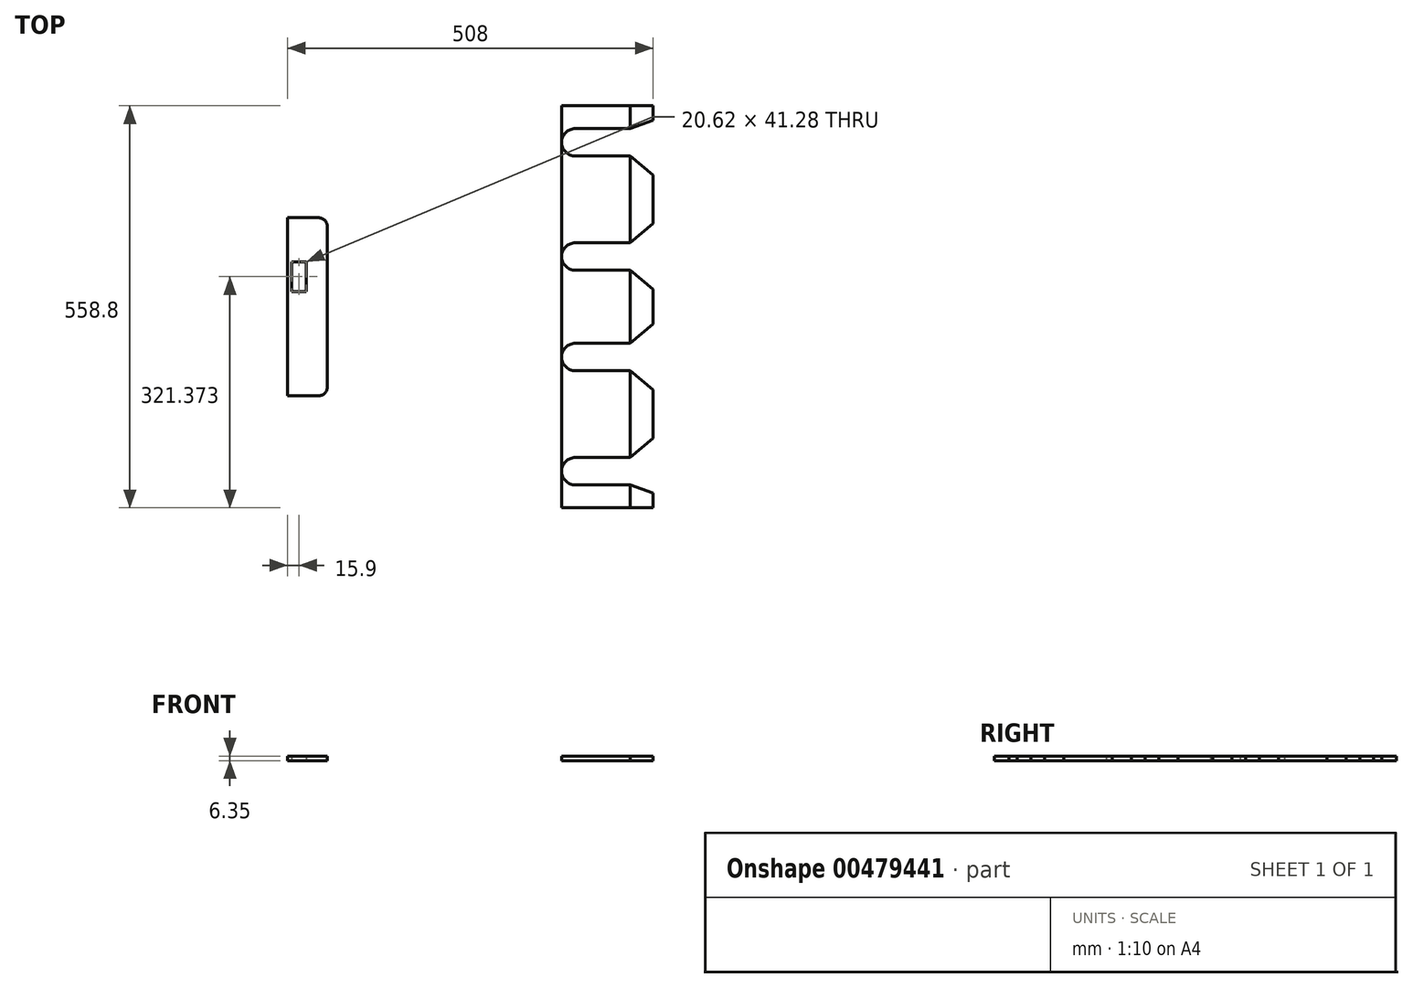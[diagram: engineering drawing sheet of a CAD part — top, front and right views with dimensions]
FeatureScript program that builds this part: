
annotation { "Feature Type Name" : "Feature", "Feature Type Description" : "" }
export const myFeature = defineFeature(function(context is Context, id is Id, definition is map)
    precondition{}
    {
        {
            var Q0;
            Q0=qCreatedBy(makeId("Top.planeOp"),FACE);
            var sketch = newSketch(context, id + "F0", { "sketchPlane" : qUnion([Q0]), "disableImprinting" : false});
            skLineSegment(sketch, "E0.bottom", {"start": v(0, 0) * mm, "end": v(508, 0) * mm});
            skLineSegment(sketch, "E0.top", {"start": v(0, 558.8) * mm, "end": v(508, 558.8) * mm});
            skLineSegment(sketch, "E0.left", {"start": v(0, 0) * mm, "end": v(0, 558.8) * mm});
            skLineSegment(sketch, "E0.right", {"start": v(508, 0) * mm, "end": v(508, 558.8) * mm});
            skLineSegment(sketch, "E1", {"start": v(55.55, 558.8) * mm, "end": v(55.55, 0) * mm});
            skLineSegment(sketch, "E2", {"start": v(381, 558.8) * mm, "end": v(381, 0) * mm});
            skLineSegment(sketch, "E3", {"start": v(212.72, 558.8) * mm, "end": v(212.72, 0) * mm});
            skLineSegment(sketch, "E4", {"start": v(0, 403.22) * mm, "end": v(55.55, 403.22) * mm});
            skLineSegment(sketch, "E5", {"start": v(0, 155.58) * mm, "end": v(55.55, 155.58) * mm});
            skLineSegment(sketch, "E6", {"start": v(55.55, 403.22) * mm, "end": v(212.72, 558.8) * mm});
            skLineSegment(sketch, "E7", {"start": v(55.55, 155.58) * mm, "end": v(212.72, 0) * mm});
            skCircle(sketch, "E8", {"center": v(400.05, 508) * mm, "radius": 19.05 * mm});
            skCircle(sketch, "E9", {"center": v(400.05, 349.25) * mm, "radius": 19.05 * mm});
            skCircle(sketch, "E10", {"center": v(400.05, 209.55) * mm, "radius": 19.05 * mm});
            skCircle(sketch, "E11", {"center": v(400.05, 50.8) * mm, "radius": 19.05 * mm});
            skLineSegment(sketch, "E12.bottom", {"start": v(508, 69.85) * mm, "end": v(400.05, 69.85) * mm});
            skLineSegment(sketch, "E12.top", {"start": v(508, 31.75) * mm, "end": v(400.05, 31.75) * mm});
            skLineSegment(sketch, "E12.left", {"start": v(508, 69.85) * mm, "end": v(508, 31.75) * mm});
            skLineSegment(sketch, "E12.right", {"start": v(400.05, 69.85) * mm, "end": v(400.05, 31.75) * mm});
            skLineSegment(sketch, "E13.bottom", {"start": v(508, 190.5) * mm, "end": v(400.05, 190.5) * mm});
            skLineSegment(sketch, "E13.top", {"start": v(508, 228.6) * mm, "end": v(400.05, 228.6) * mm});
            skLineSegment(sketch, "E13.left", {"start": v(508, 190.5) * mm, "end": v(508, 228.6) * mm});
            skLineSegment(sketch, "E13.right", {"start": v(400.05, 190.5) * mm, "end": v(400.05, 228.6) * mm});
            skLineSegment(sketch, "E14.bottom", {"start": v(508, 330.2) * mm, "end": v(400.05, 330.2) * mm});
            skLineSegment(sketch, "E14.top", {"start": v(508, 368.3) * mm, "end": v(400.05, 368.3) * mm});
            skLineSegment(sketch, "E14.left", {"start": v(508, 330.2) * mm, "end": v(508, 368.3) * mm});
            skLineSegment(sketch, "E14.right", {"start": v(400.05, 330.2) * mm, "end": v(400.05, 368.3) * mm});
            skLineSegment(sketch, "E15.bottom", {"start": v(508, 488.95) * mm, "end": v(400.05, 488.95) * mm});
            skLineSegment(sketch, "E15.top", {"start": v(508, 527.05) * mm, "end": v(400.05, 527.05) * mm});
            skLineSegment(sketch, "E15.left", {"start": v(508, 488.95) * mm, "end": v(508, 527.05) * mm});
            skLineSegment(sketch, "E15.right", {"start": v(400.05, 488.95) * mm, "end": v(400.05, 527.05) * mm});
            skLineSegment(sketch, "E16", {"start": v(476.25, 558.8) * mm, "end": v(476.25, 0) * mm});
            skPoint(sketch, "E17", {"position": v(508, 538.6) * mm});
            skPoint(sketch, "E18", {"position": v(508, 462.3) * mm});
            skPoint(sketch, "E19", {"position": v(508, 394.94) * mm});
            skPoint(sketch, "E20", {"position": v(508, 303.56) * mm});
            skPoint(sketch, "E21", {"position": v(508, 255.24) * mm});
            skPoint(sketch, "E22", {"position": v(508, 163.86) * mm});
            skPoint(sketch, "E23", {"position": v(508, 96.5) * mm});
            skPoint(sketch, "E24", {"position": v(508, 20.2) * mm});
            skPoint(sketch, "E25", {"position": v(476.25, 527.05) * mm});
            skPoint(sketch, "E26", {"position": v(476.25, 488.95) * mm});
            skPoint(sketch, "E27", {"position": v(476.25, 368.3) * mm});
            skPoint(sketch, "E28", {"position": v(476.25, 330.2) * mm});
            skPoint(sketch, "E29", {"position": v(476.25, 228.6) * mm});
            skPoint(sketch, "E30", {"position": v(476.25, 190.5) * mm});
            skPoint(sketch, "E31", {"position": v(476.25, 69.85) * mm});
            skPoint(sketch, "E32", {"position": v(476.25, 31.75) * mm});
            skLineSegment(sketch, "E33", {"start": v(476.25, 527.05) * mm, "end": v(508, 538.6) * mm});
            skLineSegment(sketch, "E34", {"start": v(476.25, 488.95) * mm, "end": v(508, 462.3) * mm});
            skLineSegment(sketch, "E35", {"start": v(508, 394.94) * mm, "end": v(476.25, 368.3) * mm});
            skLineSegment(sketch, "E36", {"start": v(476.25, 330.2) * mm, "end": v(508, 303.56) * mm});
            skLineSegment(sketch, "E37", {"start": v(508, 255.24) * mm, "end": v(476.25, 228.6) * mm});
            skLineSegment(sketch, "E38", {"start": v(476.25, 190.5) * mm, "end": v(508, 163.86) * mm});
            skLineSegment(sketch, "E39", {"start": v(476.25, 69.85) * mm, "end": v(508, 96.5) * mm});
            skLineSegment(sketch, "E40", {"start": v(476.25, 31.75) * mm, "end": v(508, 20.2) * mm});
            skLineSegment(sketch, "E41", {"start": v(82.55, 355.6) * mm, "end": v(82.55, 203.2) * mm});
            skLineSegment(sketch, "E42", {"start": v(82.55, 355.6) * mm, "end": v(247.64, 520.7) * mm});
            skLineSegment(sketch, "E43", {"start": v(339.18, 520.7) * mm, "end": v(247.64, 520.7) * mm});
            skLineSegment(sketch, "E44", {"start": v(339.18, 520.7) * mm, "end": v(339.18, 38.1) * mm});
            skLineSegment(sketch, "E45", {"start": v(247.64, 38.1) * mm, "end": v(82.55, 203.2) * mm});
            skLineSegment(sketch, "E46", {"start": v(247.64, 38.1) * mm, "end": v(339.18, 38.1) * mm});
            skLineSegment(sketch, "E47.bottom", {"start": v(5.59, 300.74) * mm, "end": v(26.21, 300.74) * mm});
            skLineSegment(sketch, "E47.top", {"start": v(5.59, 342.01) * mm, "end": v(26.21, 342.01) * mm});
            skLineSegment(sketch, "E47.left", {"start": v(5.59, 300.74) * mm, "end": v(5.59, 342.01) * mm});
            skLineSegment(sketch, "E47.right", {"start": v(26.21, 300.74) * mm, "end": v(26.21, 342.01) * mm});
            skSolve(sketch);
        }
        {
            var Q0;
            {var subQ5=sQuery(id+"F0.wireOp",EDGE,"E40");Q0=makeQuery(id+"F0.imprint","IMPRINT",FACE,{"disambiguationData":[TD([[makeQuery(id+"F0.imprint","IMPRINT",EDGE,{"derivedFrom":subQ5}),-1.0]])]});}
            var Q1;
            {var subQ5=sQuery(id+"F0.wireOp",EDGE,"E33");Q1=makeQuery(id+"F0.imprint","IMPRINT",FACE,{"disambiguationData":[TD([[makeQuery(id+"F0.imprint","IMPRINT",EDGE,{"derivedFrom":subQ5}),1.0]])]});}
            var Q2;
            {var subQ0=sQuery(id+"F0.wireOp",EDGE,"E4");Q2=makeQuery(id+"F0.imprint","IMPRINT",FACE,{"disambiguationData":[TD([[makeQuery(id+"F0.imprint","IMPRINT",EDGE,{"derivedFrom":subQ0}),-1.0]])]});}
            var Q3;
            {var subQ0=sQuery(id+"F0.wireOp",EDGE,"E38");Q3=makeQuery(id+"F0.imprint","IMPRINT",FACE,{"disambiguationData":[TD([[makeQuery(id+"F0.imprint","IMPRINT",EDGE,{"derivedFrom":subQ0}),-1.0]])]});}
            var Q4;
            {var subQ0=sQuery(id+"F0.wireOp",EDGE,"E36");Q4=makeQuery(id+"F0.imprint","IMPRINT",FACE,{"disambiguationData":[TD([[makeQuery(id+"F0.imprint","IMPRINT",EDGE,{"derivedFrom":subQ0}),-1.0]])]});}
            var Q5;
            {var subQ0=sQuery(id+"F0.wireOp",EDGE,"E34");Q5=makeQuery(id+"F0.imprint","IMPRINT",FACE,{"disambiguationData":[TD([[makeQuery(id+"F0.imprint","IMPRINT",EDGE,{"derivedFrom":subQ0}),-1.0]])]});}
            var Q6;
            {var subQ5=sQuery(id+"F0.wireOp",EDGE,"E2");var subQ7=sQuery(id+"F0.wireOp",EDGE,"E0.bottom");var subQ8=makeQuery(id+"F0.imprint","INTERSECT",VERTEX,{"derivedFrom":[subQ7,subQ5]});Q6=makeQuery(id+"F0.imprint","IMPRINT",FACE,{"disambiguationData":[TD([[makeQuery(id+"F0.imprint","IMPRINT",EDGE,{"disambiguationData":[TD([[subQ8,-1.0]])],"derivedFrom":subQ7}),1.0]])]});}
            var Q7;
            {var subQ3=sQuery(id+"F0.wireOp",EDGE,"E2");var subQ7=sQuery(id+"F0.wireOp",EDGE,"E0.top");var subQ8=makeQuery(id+"F0.imprint","INTERSECT",VERTEX,{"derivedFrom":[subQ7,subQ3]});Q7=makeQuery(id+"F0.imprint","IMPRINT",FACE,{"disambiguationData":[TD([[makeQuery(id+"F0.imprint","IMPRINT",EDGE,{"disambiguationData":[TD([[subQ8,-1.0]])],"derivedFrom":subQ7}),-1.0]])]});}
            var Q8;
            {var subQ4=sQuery(id+"F0.wireOp",EDGE,"E6");Q8=makeQuery(id+"F0.imprint","IMPRINT",FACE,{"disambiguationData":[TD([[makeQuery(id+"F0.imprint","IMPRINT",EDGE,{"derivedFrom":subQ4}),-1.0]])]});}
            var Q9;
            {var subQ17=sQuery(id+"F0.wireOp",EDGE,"E43");Q9=makeQuery(id+"F0.imprint","IMPRINT",FACE,{"disambiguationData":[TD([[makeQuery(id+"F0.imprint","IMPRINT",EDGE,{"derivedFrom":subQ17}),-1.0]])]});}
            var Q10;
            {var subQ7=sQuery(id+"F0.wireOp",EDGE,"E2");var subQ9=sQuery(id+"F0.wireOp",EDGE,"E8");var subQ11=makeQuery(id+"F0.imprint","INTERSECT",VERTEX,{"derivedFrom":[subQ7,subQ9]});Q10=makeQuery(id+"F0.imprint","IMPRINT",FACE,{"disambiguationData":[TD([[makeQuery(id+"F0.imprint","IMPRINT",EDGE,{"disambiguationData":[TD([[subQ11,-1.0]])],"derivedFrom":subQ7}),1.0]])]});}
            var Q11;
            {var subQ5=sQuery(id+"F0.wireOp",EDGE,"E2");var subQ8=sQuery(id+"F0.wireOp",EDGE,"E9");var subQ10=makeQuery(id+"F0.imprint","INTERSECT",VERTEX,{"derivedFrom":[subQ5,subQ8]});Q11=makeQuery(id+"F0.imprint","IMPRINT",FACE,{"disambiguationData":[TD([[makeQuery(id+"F0.imprint","IMPRINT",EDGE,{"disambiguationData":[TD([[subQ10,-1.0]])],"derivedFrom":subQ5}),1.0]])]});}
            var Q12;
            {var subQ5=sQuery(id+"F0.wireOp",EDGE,"E10");var subQ6=sQuery(id+"F0.wireOp",EDGE,"E2");var subQ7=makeQuery(id+"F0.imprint","INTERSECT",VERTEX,{"derivedFrom":[subQ6,subQ5]});Q12=makeQuery(id+"F0.imprint","IMPRINT",FACE,{"disambiguationData":[TD([[makeQuery(id+"F0.imprint","IMPRINT",EDGE,{"disambiguationData":[TD([[subQ7,-1.0]])],"derivedFrom":subQ6}),1.0]])]});}
            extrude(context, id + "F1", {"entities" : qUnion([Q0, Q1, Q2, Q3, Q4, Q5, Q6, Q7, Q8, Q9, Q10, Q11, Q12]), "depth" : 6.35 * mm, "flatOperationType" : FlatOperationType.REMOVE, "offsetDistance" : 25.4 * mm, "domain" : OperationDomain.MODEL});
        }
        {
            var Q0;
            Q0=makeQuery(id+"F1.opExtrude","SWEPT_EDGE",EDGE,{"disambiguationData":[OSD([sQuery(id+"F0.wireOp",EDGE,"E43"),sQuery(id+"F0.wireOp",EDGE,"E44")])]});
            var Q1;
            Q1=makeQuery(id+"F1.opExtrude","SWEPT_EDGE",EDGE,{"disambiguationData":[OSD([sQuery(id+"F0.wireOp",EDGE,"E44"),sQuery(id+"F0.wireOp",EDGE,"E46")])]});
            var Q2;
            Q2=makeQuery(id+"F1.opExtrude","SWEPT_EDGE",EDGE,{"disambiguationData":[OSD([sQuery(id+"F0.wireOp",EDGE,"E45"),sQuery(id+"F0.wireOp",EDGE,"E46")])]});
            var Q3;
            Q3=makeQuery(id+"F1.opExtrude","SWEPT_EDGE",EDGE,{"disambiguationData":[OSD([sQuery(id+"F0.wireOp",EDGE,"E41"),sQuery(id+"F0.wireOp",EDGE,"E45")])]});
            var Q4;
            Q4=makeQuery(id+"F1.opExtrude","SWEPT_EDGE",EDGE,{"disambiguationData":[OSD([sQuery(id+"F0.wireOp",EDGE,"E41"),sQuery(id+"F0.wireOp",EDGE,"E42")])]});
            var Q5;
            Q5=makeQuery(id+"F1.opExtrude","SWEPT_EDGE",EDGE,{"disambiguationData":[OSD([sQuery(id+"F0.wireOp",EDGE,"E42"),sQuery(id+"F0.wireOp",EDGE,"E43")])]});
            var Q6;
            Q6=makeQuery(id+"F1.opExtrude","SWEPT_EDGE",EDGE,{"disambiguationData":[OSD([sQuery(id+"F0.wireOp",EDGE,"E1"),sQuery(id+"F0.wireOp",EDGE,"E5"),sQuery(id+"F0.wireOp",EDGE,"E7")])]});
            var Q7;
            Q7=makeQuery(id+"F1.opExtrude","SWEPT_EDGE",EDGE,{"disambiguationData":[OSD([sQuery(id+"F0.wireOp",EDGE,"E1"),sQuery(id+"F0.wireOp",EDGE,"E4"),sQuery(id+"F0.wireOp",EDGE,"E6")])]});
            fillet(context, id + "F2", {"entities" : qUnion([Q0, Q1, Q2, Q3, Q4, Q5, Q6, Q7]), "radius" : 12.7 * mm, "tangentPropagation" : true, "allowEdgeOverflow" : false});
        }
    });
